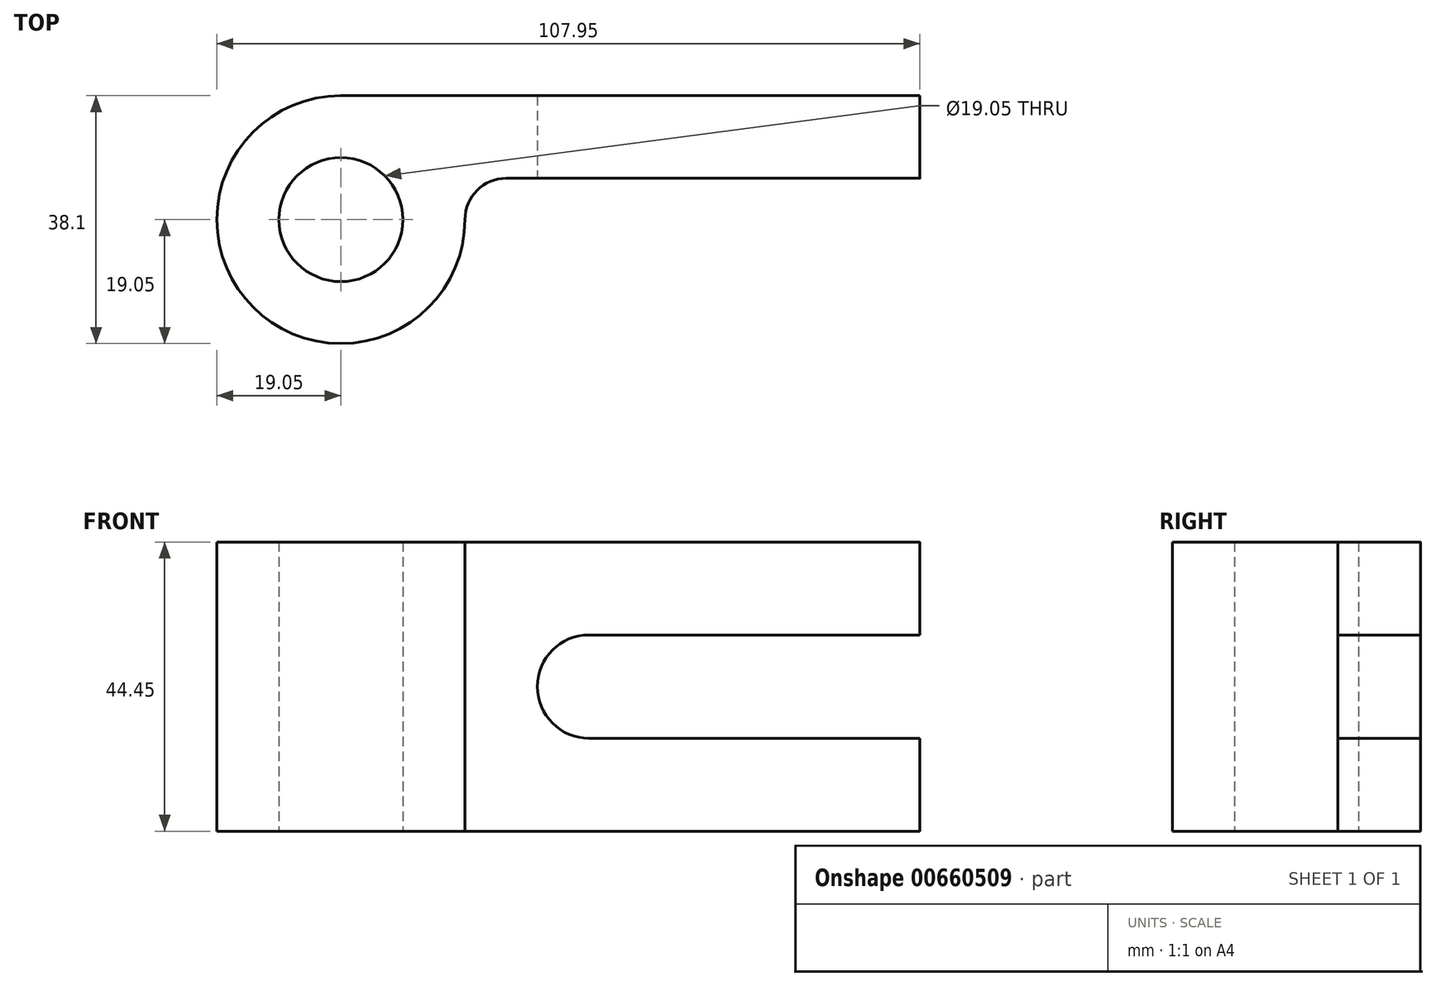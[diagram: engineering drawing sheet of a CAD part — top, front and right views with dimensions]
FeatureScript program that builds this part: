
annotation { "Feature Type Name" : "Feature", "Feature Type Description" : "" }
export const myFeature = defineFeature(function(context is Context, id is Id, definition is map)
    precondition{}
    {
        {
            var Q0;
            Q0=qCreatedBy(makeId("Top.planeOp"),FACE);
            var sketch = newSketch(context, id + "F0", { "sketchPlane" : qUnion([Q0])});
            skArc(sketch, "E0", {"start": v(0, 19.05) * mm, "mid": v(-11, -15.55) * mm, "end": v(17.96, 6.35) * mm});
            skLineSegment(sketch, "E1.bottom", {"start": v(0, 19.05) * mm, "end": v(88.9, 19.05) * mm});
            skLineSegment(sketch, "E1.top", {"start": v(17.96, 6.35) * mm, "end": v(88.9, 6.35) * mm});
            skLineSegment(sketch, "E1.right", {"start": v(88.9, 19.05) * mm, "end": v(88.9, 6.35) * mm});
            skCircle(sketch, "E2", {"center": v(0, 0) * mm, "radius": 9.53 * mm});
            skSolve(sketch);
        }
        {
            var Q0;
            Q0 = qSketchRegion(id + "F0", true);
            extrude(context, id + "F1", {"entities" : qUnion([Q0]), "depth" : 44.45 * mm, "offsetDistance" : 25.4 * mm});
        }
        {
            var Q0;
            Q0=qCreatedBy(makeId("Front.planeOp"),FACE);
            var sketch = newSketch(context, id + "F2", { "sketchPlane" : qUnion([Q0])});
            skLineSegment(sketch, "E3.bottom", {"start": v(88.9, 30.16) * mm, "end": v(38.1, 30.16) * mm});
            skLineSegment(sketch, "E3.top", {"start": v(88.9, 14.29) * mm, "end": v(38.1, 14.29) * mm});
            skArc(sketch, "E4", {"start": v(38.1, 30.16) * mm, "mid": v(30.16, 22.23) * mm, "end": v(38.1, 14.29) * mm});
            skLineSegment(sketch, "E5", {"start": v(88.9, 30.16) * mm, "end": v(88.9, 14.29) * mm});
            skSolve(sketch);
        }
        {
            var Q0;
            Q0 = qSketchRegion(id + "F2", true);
            extrude(context, id + "F3", {"entities" : qUnion([Q0]), "operationType" : NewBodyOperationType.REMOVE, "endBound" : BoundingType.THROUGH_ALL, "oppositeDirection" : true, "depth" : 25.4 * mm, "offsetDistance" : 25.4 * mm});
        }
        {
            var Q0;
            Q0=makeQuery(id+"F1.opExtrude","CAP_EDGE",EDGE,{"disambiguationData":[OSD([sQuery(id+"F0.wireOp",EDGE,"E1.right")])],"isStart":false});
            var Q1;
            Q1=makeQuery(id+"F1.opExtrude","CAP_EDGE",EDGE,{"disambiguationData":[OSD([sQuery(id+"F0.wireOp",EDGE,"E1.right")])],"isStart":true});
            fillet(context, id + "F4", {"entities" : qUnion([Q0, Q1]), "radius" : 3 / 203.2 * mm, "tangentPropagation" : true, "allowEdgeOverflow" : false});
        }
        {
            var Q0;
            Q0=makeQuery(id+"F1.opExtrude","SWEPT_EDGE",EDGE,{"disambiguationData":[OSD([sQuery(id+"F0.wireOp",EDGE,"E0"),sQuery(id+"F0.wireOp",EDGE,"E1.top")])]});
            fillet(context, id + "F5", {"entities" : qUnion([Q0]), "radius" : 6.35 * mm, "tangentPropagation" : true, "allowEdgeOverflow" : false});
        }
    });
